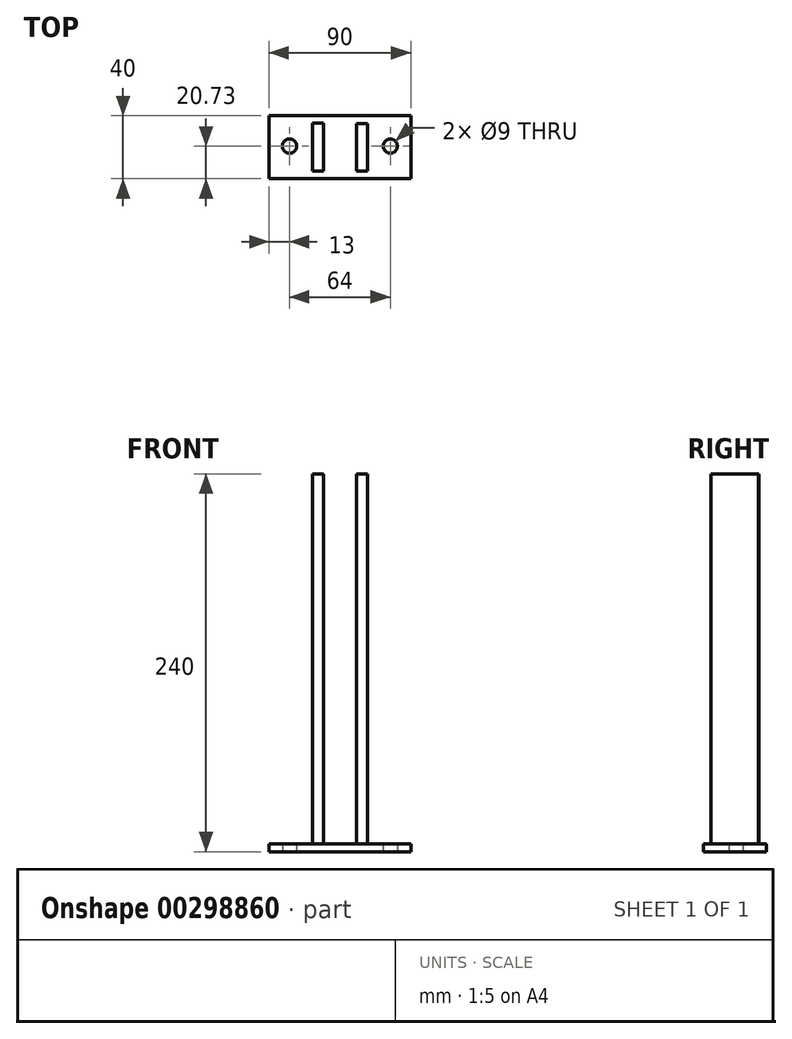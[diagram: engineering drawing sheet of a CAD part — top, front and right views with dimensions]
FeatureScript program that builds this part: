
annotation { "Feature Type Name" : "Feature", "Feature Type Description" : "" }
export const myFeature = defineFeature(function(context is Context, id is Id, definition is map)
    precondition{}
    {
        {
            var Q0;
            Q0=qCreatedBy(makeId("Right.planeOp"),FACE);
            var sketch = newSketch(context, id + "F0", { "sketchPlane" : qUnion([Q0])});
            skLineSegment(sketch, "E0.bottom", {"start": v(-20.73, 5) * mm, "end": v(19.27, 5) * mm});
            skLineSegment(sketch, "E0.left", {"start": v(-20.73, 5) * mm, "end": v(-20.73, 0) * mm});
            skLineSegment(sketch, "E0.right", {"start": v(19.27, 5) * mm, "end": v(19.27, 0) * mm});
            skLineSegment(sketch, "E1.trimOffspring", {"start": v(-20.73, 0) * mm, "end": v(19.27, 0) * mm});
            skSolve(sketch);
        }
        {
            var Q0;
            {var subQ3=sQuery(id+"F0.wireOp",EDGE,"ff7b447e-6627-4066-b775-27bb9192647b.left");Q0=makeQuery(id+"F0.imprint","IMPRINT",FACE,{"disambiguationData":[TD([[makeQuery(id+"F0.imprint","IMPRINT",EDGE,{"derivedFrom":subQ3}),-1.0]])]});}
            var Q1;
            {var subQ3=sQuery(id+"F0.wireOp",EDGE,"ff7b447e-6627-4066-b775-27bb9192647b.right");Q1=makeQuery(id+"F0.imprint","IMPRINT",FACE,{"disambiguationData":[TD([[makeQuery(id+"F0.imprint","IMPRINT",EDGE,{"derivedFrom":subQ3}),1.0]])]});}
            var Q2;
            {var subQ0=sQuery(id+"F0.wireOp",EDGE,"ff7b447e-6627-4066-b775-27bb9192647b.top");Q2=makeQuery(id+"F0.imprint","IMPRINT",FACE,{"disambiguationData":[TD([[makeQuery(id+"F0.imprint","IMPRINT",EDGE,{"derivedFrom":subQ0}),-1.0]])]});}
            var Q3;
            {var subQ5=sQuery(id+"F0.wireOp",EDGE,"E0.left");Q3=makeQuery(id+"F0.imprint","IMPRINT",FACE,{"disambiguationData":[TD([[makeQuery(id+"F0.imprint","IMPRINT",EDGE,{"derivedFrom":subQ5}),1.0]])]});}
            var Q4;
            {var subQ5=sQuery(id+"F0.wireOp",EDGE,"E0.right");Q4=makeQuery(id+"F0.imprint","IMPRINT",FACE,{"disambiguationData":[TD([[makeQuery(id+"F0.imprint","IMPRINT",EDGE,{"derivedFrom":subQ5}),-1.0]])]});}
            extrude(context, id + "F1", {"entities" : qUnion([Q0, Q1, Q2, Q3, Q4]), "depth" : 90 * mm});
        }
        {
            var Q0;
            Q0=qCreatedBy(makeId("Top.planeOp"),FACE);
            var sketch = newSketch(context, id + "F2", { "sketchPlane" : qUnion([Q0])});
            skLineSegment(sketch, "E2.bottom", {"start": v(27.5, 14.5) * mm, "end": v(34.5, 14.5) * mm});
            skLineSegment(sketch, "E2.top", {"start": v(27.5, -15.98) * mm, "end": v(34.5, -15.98) * mm});
            skLineSegment(sketch, "E2.left", {"start": v(27.5, 14.5) * mm, "end": v(27.5, -15.98) * mm});
            skLineSegment(sketch, "E2.right", {"start": v(34.5, 14.5) * mm, "end": v(34.5, -15.98) * mm});
            skLineSegment(sketch, "E3.bottom", {"start": v(55.5, 14.27) * mm, "end": v(62.5, 14.27) * mm});
            skLineSegment(sketch, "E3.top", {"start": v(55.5, -15.73) * mm, "end": v(62.5, -15.73) * mm});
            skLineSegment(sketch, "E3.left", {"start": v(55.5, 14.27) * mm, "end": v(55.5, -15.73) * mm});
            skLineSegment(sketch, "E3.right", {"start": v(62.5, 14.27) * mm, "end": v(62.5, -15.73) * mm});
            skLineSegment(sketch, "E4", {"start": v(0, -20.73) * mm, "end": v(90, -20.73) * mm, "construction": true});
            skLineSegment(sketch, "E5", {"start": v(90, 19.27) * mm, "end": v(90, -20.73) * mm, "construction": true});
            skPoint(sketch, "E6.center.orphan", {"position": v(77, 0) * mm});
            skPoint(sketch, "E7.center.orphan", {"position": v(13, 0) * mm});
            skSolve(sketch);
        }
        {
            var Q0;
            Q0=qSketchRegion(id+"F2",true);
            extrude(context, id + "F3", {"entities" : qUnion([Q0]), "operationType" : NewBodyOperationType.ADD, "depth" : 240 * mm});
        }
        {
            var Q0;
            Q0=qCreatedBy(makeId("Top.planeOp"),FACE);
            var sketch = newSketch(context, id + "F4", { "sketchPlane" : qUnion([Q0])});
            skCircle(sketch, "E8", {"center": v(77, 0) * mm, "radius": 4.5 * mm});
            skCircle(sketch, "E9", {"center": v(13, 0) * mm, "radius": 4.5 * mm});
            skSolve(sketch);
        }
        {
            var Q0;
            Q0=sQuery(id+"F4.wireOp",VERTEX,"E9.center");
            var Q1;
            Q1=sQuery(id+"F4.wireOp",VERTEX,"E8.center");
            var Q2;
            Q2=makeQuery(id+"F1.opExtrude","SWEPT_BODY",BODY,{"disambiguationData":[OSD([sQuery(id+"F0.wireOp",EDGE,"E0.bottom"),sQuery(id+"F0.wireOp",EDGE,"E0.left"),sQuery(id+"F0.wireOp",EDGE,"E0.right"),sQuery(id+"F0.wireOp",EDGE,"E1.trimOffspring")])]});
            hole(context, id + "F5", {"style" : HoleStyle.SIMPLE, "endStyle" : HoleEndStyle.THROUGH, "oppositeDirection" : true, "holeDiameter" : 9 * mm, "tappedDepth" : 12 * mm, "tapClearance" : 3, "locations" : qUnion([Q0, Q1]), "scope" : qUnion([Q2])});
        }
    });
